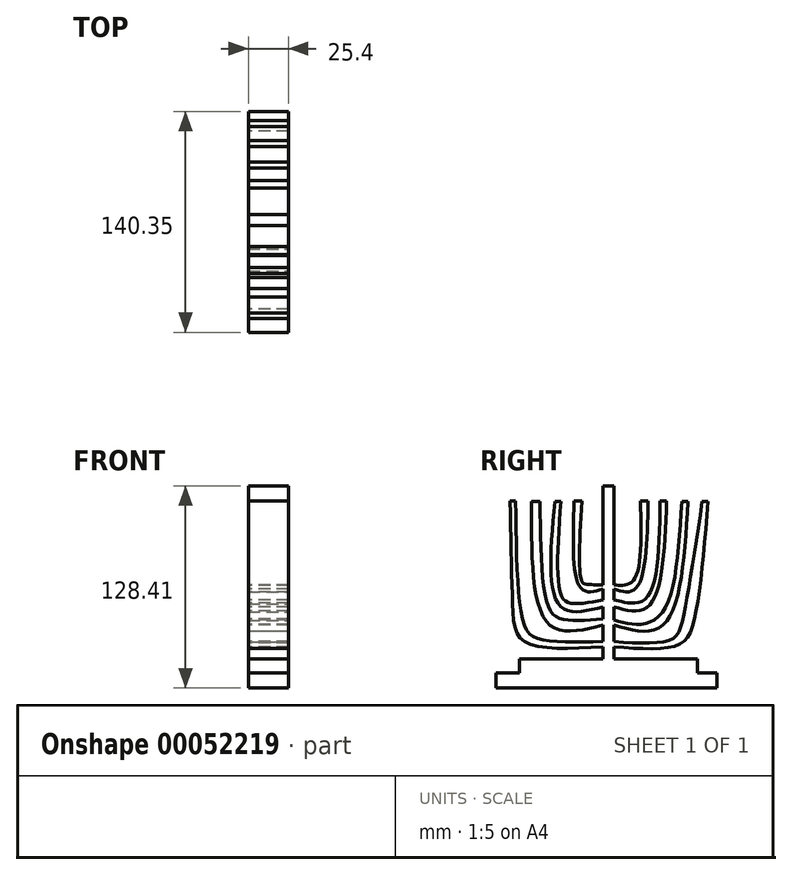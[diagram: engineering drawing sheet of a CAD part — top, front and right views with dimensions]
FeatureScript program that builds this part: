
annotation { "Feature Type Name" : "Feature", "Feature Type Description" : "" }
export const myFeature = defineFeature(function(context is Context, id is Id, definition is map)
    precondition{}
    {
        {
            var Q0;
            Q0=qCreatedBy(makeId("Right.planeOp"),FACE);
            var sketch = newSketch(context, id + "F0", { "sketchPlane" : qUnion([Q0])});
            skLineSegment(sketch, "E0.bottom", {"start": v(69, -62.89) * mm, "end": v(-71.35, -62.89) * mm});
            skLineSegment(sketch, "E0.left", {"start": v(69, -62.89) * mm, "end": v(69, -53.33) * mm});
            skLineSegment(sketch, "E0.right", {"start": v(-71.35, -62.89) * mm, "end": v(-71.35, -53.33) * mm});
            skLineSegment(sketch, "E1.top", {"start": v(56.47, -44.46) * mm, "end": v(-56.47, -44.46) * mm});
            skLineSegment(sketch, "E1.left", {"start": v(56.47, -53.33) * mm, "end": v(56.47, -44.46) * mm});
            skLineSegment(sketch, "E2", {"start": v(3.53, -44.46) * mm, "end": v(3.53, 55.53) * mm});
            skLineSegment(sketch, "E3", {"start": v(-3.53, 55.53) * mm, "end": v(-3.53, -44.46) * mm});
            skFitSpline(sketch, "E4", {"points": [v(3.53, -36.72) * mm, v(44.07, -35.55) * mm, v(54.06, -21.25) * mm, v(63.26, 55.53) * mm], "startDerivative": vector(145.78, -10.82) * mm, "endDerivative": vector(16.47, 200.45) * mm});
            skLineSegment(sketch, "E5", {"start": v(63.26, 55.53) * mm, "end": v(59.54, 55.53) * mm});
            skFitSpline(sketch, "E6", {"points": [v(59.54, 55.53) * mm, v(47, -20.08) * mm, v(39.96, -32.02) * mm, v(3.53, -33.4) * mm], "startDerivative": vector(-28.71, -192.4) * mm, "endDerivative": vector(-135.72, 8.59) * mm});
            skFitSpline(sketch, "E7", {"points": [v(3.53, -22.82) * mm, v(34.08, -23.4) * mm, v(50.53, 55.72) * mm], "startDerivative": vector(90.46, -26.17) * mm, "endDerivative": vector(9.95, 167.83) * mm});
            skLineSegment(sketch, "E8", {"start": v(50.53, 55.72) * mm, "end": v(46.62, 55.72) * mm});
            skFitSpline(sketch, "E9", {"points": [v(46.62, 55.72) * mm, v(35.06, -13.61) * mm, v(19.59, -22.43) * mm, v(3.53, -19.68) * mm], "startDerivative": vector(-10.17, -169.26) * mm, "endDerivative": vector(-65.9, 18.67) * mm});
            skFitSpline(sketch, "E10", {"points": [v(3.53, -11.26) * mm, v(25.07, -11.26) * mm, v(37.02, 55.92) * mm], "startDerivative": vector(67.3, -18.87) * mm, "endDerivative": vector(5.46, 138.52) * mm});
            skLineSegment(sketch, "E11", {"start": v(37.02, 55.92) * mm, "end": v(32.9, 55.92) * mm});
            skFitSpline(sketch, "E12", {"points": [v(32.9, 55.92) * mm, v(23.9, -5.97) * mm, v(11.16, -8.52) * mm, v(3.53, -6.76) * mm], "startDerivative": vector(-2.83, -146.68) * mm, "endDerivative": vector(-35.18, 9.74) * mm});
            skFitSpline(sketch, "E13", {"points": [v(3.53, 0) * mm, v(17.04, 0) * mm, v(25.27, 56.11) * mm], "startDerivative": vector(45.95, -13.7) * mm, "endDerivative": vector(2.51, 111.56) * mm});
            skLineSegment(sketch, "E14", {"start": v(25.27, 56.11) * mm, "end": v(20.37, 56.11) * mm});
            skFitSpline(sketch, "E15", {"points": [v(20.37, 56.11) * mm, v(17.04, 7.34) * mm, v(9.99, 2.45) * mm, v(3.53, 2.64) * mm], "startDerivative": vector(2.73, -109.06) * mm, "endDerivative": vector(-31.23, 3.87) * mm});
            skFitSpline(sketch, "E16", {"points": [v(-3.53, -36.72) * mm, v(-53.86, -33) * mm, v(-60.72, -12.24) * mm, v(-62.48, 56.11) * mm], "startDerivative": vector(-175.87, -9.72) * mm, "endDerivative": vector(-3.36, 185.99) * mm});
            skLineSegment(sketch, "E17", {"start": v(-62.48, 56.11) * mm, "end": v(-58.95, 56.11) * mm});
            skFitSpline(sketch, "E18", {"points": [v(-58.95, 56.11) * mm, v(-53.67, -22.23) * mm, v(-44.46, -31.44) * mm, v(-3.53, -33.4) * mm], "startDerivative": vector(2.57, -207.36) * mm, "endDerivative": vector(142.73, 2.5) * mm});
            skFitSpline(sketch, "E19", {"points": [v(-3.53, -22.82) * mm, v(-37.21, -22.82) * mm, v(-48.77, 55.72) * mm], "startDerivative": vector(-98.48, -25.58) * mm, "endDerivative": vector(1, 168.98) * mm});
            skLineSegment(sketch, "E20", {"start": v(-48.77, 55.72) * mm, "end": v(-43.48, 55.72) * mm});
            skFitSpline(sketch, "E21", {"points": [v(-43.48, 55.72) * mm, v(-37.6, -12.24) * mm, v(-28, -19.3) * mm, v(-3.53, -19.1) * mm], "startDerivative": vector(2, -171.96) * mm, "endDerivative": vector(91.85, 6.59) * mm});
            skFitSpline(sketch, "E22", {"points": [v(-3.53, -11.26) * mm, v(-30.16, -11.26) * mm, v(-34.08, 55.53) * mm], "startDerivative": vector(-80.94, -21.07) * mm, "endDerivative": vector(12.76, 142.33) * mm});
            skLineSegment(sketch, "E23", {"start": v(-34.08, 55.53) * mm, "end": v(-30.16, 55.53) * mm});
            skFitSpline(sketch, "E24", {"points": [v(-30.16, 55.53) * mm, v(-30.16, -3.43) * mm, v(-23.11, -9.1) * mm, v(-3.53, -6.76) * mm], "startDerivative": vector(-10.77, -145.82) * mm, "endDerivative": vector(74.78, 15.44) * mm});
            skFitSpline(sketch, "E25", {"points": [v(-3.53, 0) * mm, v(-16.84, 0) * mm, v(-21.74, 55.92) * mm], "startDerivative": vector(-46.13, -13.62) * mm, "endDerivative": vector(3.94, 111.12) * mm});
            skLineSegment(sketch, "E26", {"start": v(-21.74, 55.92) * mm, "end": v(-16.84, 55.92) * mm});
            skFitSpline(sketch, "E27", {"points": [v(-16.84, 55.92) * mm, v(-16.84, 4.8) * mm, v(-13.71, 3.04) * mm, v(-3.53, 2.64) * mm], "startDerivative": vector(-6.74, -117.45) * mm, "endDerivative": vector(44.39, -0.9) * mm});
            skLineSegment(sketch, "E28", {"start": v(69, -53.33) * mm, "end": v(56.47, -53.33) * mm});
            skLineSegment(sketch, "E29", {"start": v(3.53, 55.53) * mm, "end": v(3.53, 65.52) * mm});
            skLineSegment(sketch, "E30", {"start": v(3.53, 65.52) * mm, "end": v(-3.53, 65.52) * mm});
            skLineSegment(sketch, "E31", {"start": v(-3.53, 65.52) * mm, "end": v(-3.53, 55.53) * mm});
            skLineSegment(sketch, "E32", {"start": v(-56.47, -44.46) * mm, "end": v(-56.47, -53.33) * mm});
            skLineSegment(sketch, "E33", {"start": v(-56.47, -53.33) * mm, "end": v(-71.35, -53.33) * mm});
            skSolve(sketch);
        }
        {
            var Q0;
            Q0 = qSketchRegion(id + "F0", true);
            extrude(context, id + "F1", {"entities" : qUnion([Q0]), "depth" : 25.4 * mm});
        }
    });
